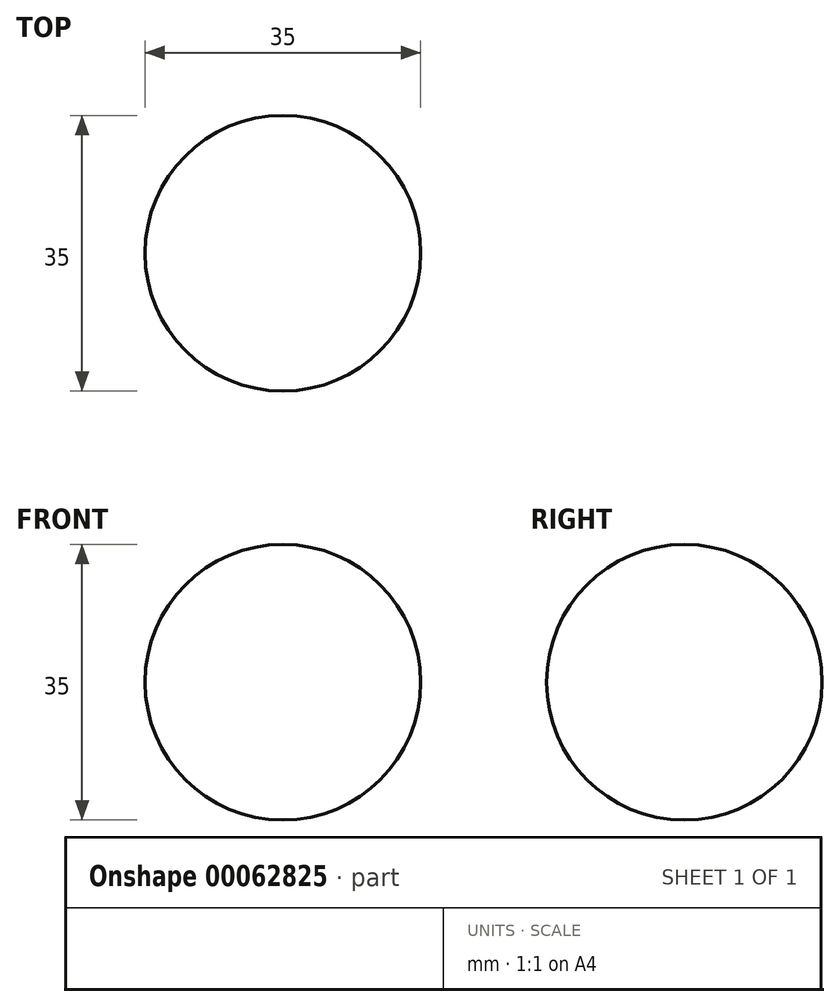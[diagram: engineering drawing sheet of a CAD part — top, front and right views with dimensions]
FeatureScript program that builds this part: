
annotation { "Feature Type Name" : "Feature", "Feature Type Description" : "" }
export const myFeature = defineFeature(function(context is Context, id is Id, definition is map)
    precondition{}
    {
        {
            var Q0;
            Q0=qCreatedBy(makeId("Top.planeOp"),FACE);
            var sketch = newSketch(context, id + "F0", { "sketchPlane" : qUnion([Q0])});
            skArc(sketch, "E0", {"start": v(0, -17.5) * mm, "mid": v(17.5, 0) * mm, "end": v(0, 17.5) * mm});
            skLineSegment(sketch, "E1", {"start": v(0, 17.5) * mm, "end": v(0, -17.5) * mm});
            skSolve(sketch);
        }
        {
            var Q0;
            Q0=makeQuery(id+"F0.imprint","IMPRINT",FACE,{"disambiguationData":[TD([[makeQuery(id+"F0.imprint","IMPRINT",EDGE,{"derivedFrom":sQuery(id+"F0.wireOp",EDGE,"E0")}),1.0]])]});
            var Q1;
            Q1=sQuery(id+"F0.wireOp",EDGE,"E1");
            revolve(context, id + "F1", {"entities" : qUnion([Q0]), "axis" : qUnion([Q1]), "revolveType" : RevolveType.FULL});
        }
    });
